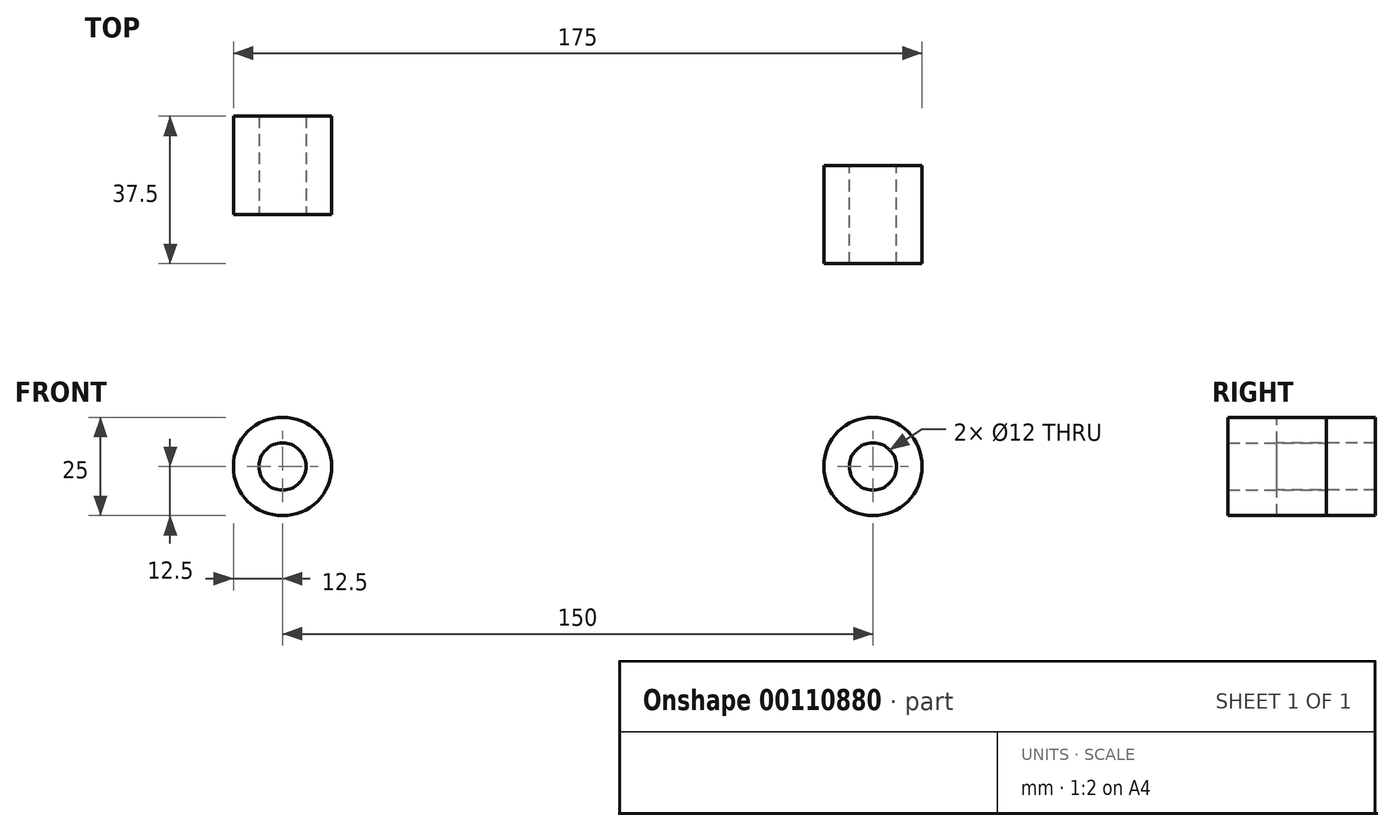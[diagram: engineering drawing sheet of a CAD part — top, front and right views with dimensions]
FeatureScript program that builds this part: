
annotation { "Feature Type Name" : "Feature", "Feature Type Description" : "" }
export const myFeature = defineFeature(function(context is Context, id is Id, definition is map)
    precondition{}
    {
        {
            var Q0;
            Q0=qCreatedBy(makeId("Front.planeOp"),FACE);
            var sketch = newSketch(context, id + "F0", { "sketchPlane" : qUnion([Q0])});
            skCircle(sketch, "E0", {"center": v(0, 0) * mm, "radius": 12.5 * mm});
            skCircle(sketch, "E1", {"center": v(0, 0) * mm, "radius": 6 * mm});
            skSolve(sketch);
        }
        {
            var Q0;
            Q0=makeQuery(id+"F0.imprint","IMPRINT",FACE,{"disambiguationData":[TD([[makeQuery(id+"F0.imprint","IMPRINT",EDGE,{"derivedFrom":sQuery(id+"F0.wireOp",EDGE,"E0")}),1.0]])]});
            extrude(context, id + "F1", {"entities" : qUnion([Q0]), "oppositeDirection" : true, "depth" : 25 * mm});
        }
        {
            var Q0;
            Q0=qCreatedBy(makeId("Front.planeOp"),FACE);
            var sketch = newSketch(context, id + "F2", { "sketchPlane" : qUnion([Q0])});
            skLineSegment(sketch, "E2", {"start": v(0, 0) * mm, "end": v(150, 0) * mm, "construction": true});
            skCircle(sketch, "E3", {"center": v(150, 0) * mm, "radius": 12.5 * mm});
            skCircle(sketch, "E4", {"center": v(150, 0) * mm, "radius": 6 * mm});
            skSolve(sketch);
        }
        {
            var Q0;
            Q0=makeQuery(id+"F2.imprint","IMPRINT",FACE,{"disambiguationData":[TD([[makeQuery(id+"F2.imprint","IMPRINT",EDGE,{"derivedFrom":sQuery(id+"F2.wireOp",EDGE,"E3")}),1.0]])]});
            extrude(context, id + "F3", {"entities" : qUnion([Q0]), "endBound" : BoundingType.SYMMETRIC, "depth" : 25 * mm});
        }
    });
